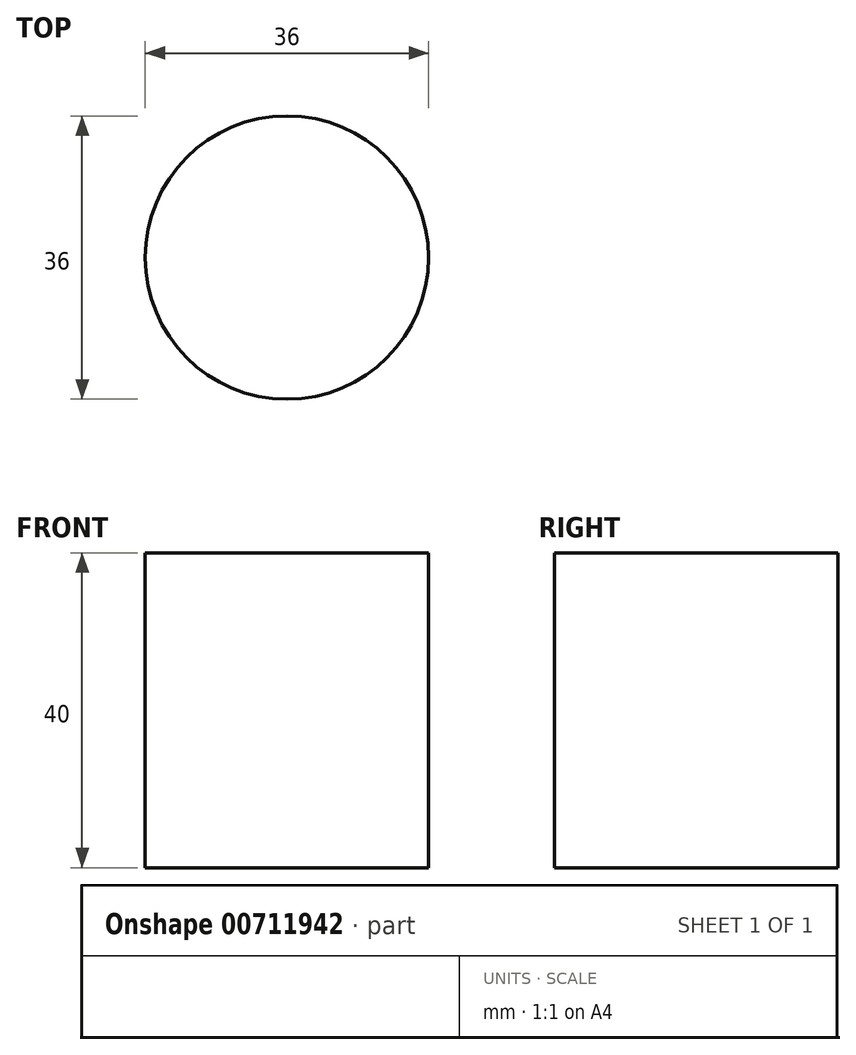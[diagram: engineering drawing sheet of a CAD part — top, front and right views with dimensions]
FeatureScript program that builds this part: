
annotation { "Feature Type Name" : "Feature", "Feature Type Description" : "" }
export const myFeature = defineFeature(function(context is Context, id is Id, definition is map)
    precondition{}
    {
        {
            var Q0;
            Q0=qCreatedBy(makeId("Top.planeOp"),FACE);
            var sketch = newSketch(context, id + "F0", { "sketchPlane" : qUnion([Q0])});
            skCircle(sketch, "E0", {"center": v(0, 0) * mm, "radius": 18 * mm});
            skSolve(sketch);
        }
        {
            var Q0;
            Q0 = qSketchRegion(id + "F0", true);
            extrude(context, id + "F1", {"entities" : qUnion([Q0]), "depth" : 40 * mm, "offsetDistance" : 25 * mm});
        }
    });
